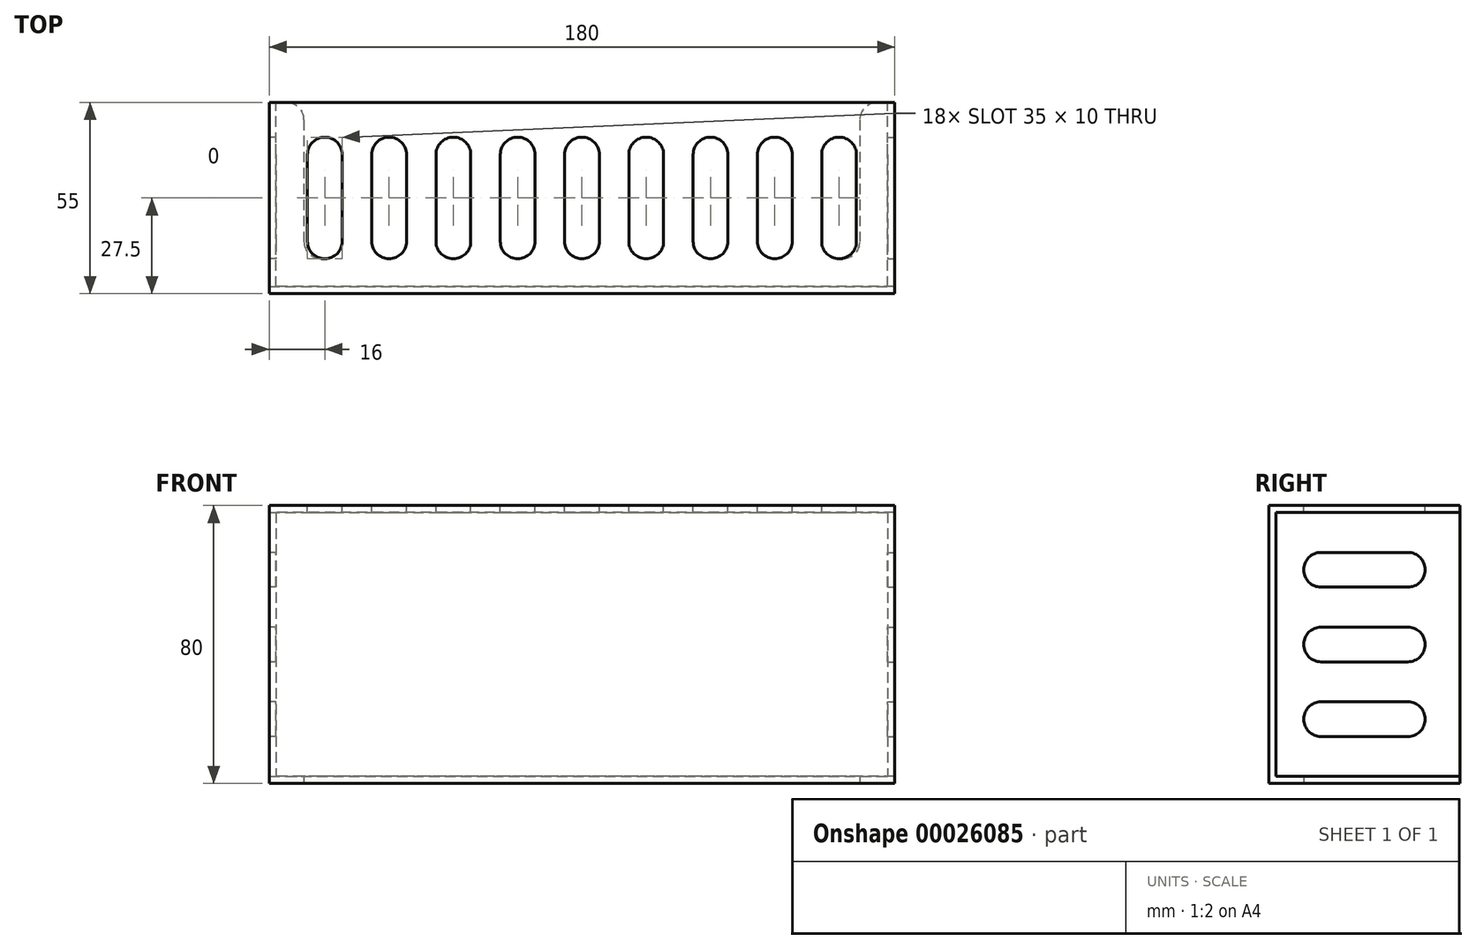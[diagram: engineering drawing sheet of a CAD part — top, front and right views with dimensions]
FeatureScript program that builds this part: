
annotation { "Feature Type Name" : "Feature", "Feature Type Description" : "" }
export const myFeature = defineFeature(function(context is Context, id is Id, definition is map)
    precondition{}
    {
        {
            var Q0;
            Q0=qCreatedBy(makeId("Top.planeOp"),FACE);
            var sketch = newSketch(context, id + "F0", { "sketchPlane" : qUnion([Q0])});
            skLineSegment(sketch, "E0.bottom", {"start": v(0, 0) * mm, "end": v(5, 0) * mm});
            skLineSegment(sketch, "E0.top", {"start": v(0, -55) * mm, "end": v(180, -55) * mm});
            skLineSegment(sketch, "E0.left", {"start": v(0, 0) * mm, "end": v(0, -55) * mm});
            skLineSegment(sketch, "E0.right", {"start": v(180, 0) * mm, "end": v(180, -55) * mm});
            skLineSegment(sketch, "E1.0", {"start": v(10, -5) * mm, "end": v(10, -40) * mm});
            skLineSegment(sketch, "E2.0", {"start": v(170, -5) * mm, "end": v(170, -40) * mm});
            skLineSegment(sketch, "E3.0", {"start": v(15, -45) * mm, "end": v(165, -45) * mm});
            skLineSegment(sketch, "E4.trimOffspring", {"start": v(175, 0) * mm, "end": v(180, 0) * mm});
            skPoint(sketch, "E5.visualSharp", {"position": v(10, 0) * mm});
            skArc(sketch, "E5.filletArc", {"start": v(10, -5) * mm, "mid": v(8.54, -1.46) * mm, "end": v(5, 0) * mm});
            skPoint(sketch, "E6.visualSharp", {"position": v(170, 0) * mm});
            skArc(sketch, "E6.filletArc", {"start": v(175, 0) * mm, "mid": v(171.46, -1.46) * mm, "end": v(170, -5) * mm});
            skPoint(sketch, "E7.visualSharp", {"position": v(10, -45) * mm});
            skArc(sketch, "E7.filletArc", {"start": v(10, -40) * mm, "mid": v(11.46, -43.54) * mm, "end": v(15, -45) * mm});
            skPoint(sketch, "E8.visualSharp", {"position": v(170, -45) * mm});
            skArc(sketch, "E8.filletArc", {"start": v(165, -45) * mm, "mid": v(168.54, -43.54) * mm, "end": v(170, -40) * mm});
            skSolve(sketch);
        }
        {
            var Q0;
            Q0=makeQuery(id+"F0.imprint","IMPRINT",FACE,{"disambiguationData":[TD([[makeQuery(id+"F0.imprint","IMPRINT",EDGE,{"derivedFrom":sQuery(id+"F0.wireOp",EDGE,"E0.bottom")}),-1.0]])]});
            extrude(context, id + "F1", {"entities" : qUnion([Q0]), "depth" : 2 * mm});
        }
        {
            var Q0;
            Q0=makeQuery(id+"F1.opExtrude","SWEPT_FACE",FACE,{"disambiguationData":[OSD([sQuery(id+"F0.wireOp",EDGE,"E0.top")])]});
            var sketch = newSketch(context, id + "F2", { "sketchPlane" : qUnion([Q0])});
            skLineSegment(sketch, "E9.0", {"start": v(0, 2) * mm, "end": v(0, 0) * mm});
            skLineSegment(sketch, "E10.0", {"start": v(0, 0) * mm, "end": v(180, 0) * mm});
            skLineSegment(sketch, "E11.0", {"start": v(180, 2) * mm, "end": v(180, 0) * mm});
            skLineSegment(sketch, "E12.top", {"start": v(0, 80) * mm, "end": v(180, 80) * mm});
            skLineSegment(sketch, "E12.left", {"start": v(0, 0) * mm, "end": v(0, 80) * mm});
            skLineSegment(sketch, "E12.right", {"start": v(180, 0) * mm, "end": v(180, 80) * mm});
            skSolve(sketch);
        }
        {
            var Q0;
            {var subQ1=sQuery(id+"F2.wireOp",EDGE,"E12.top");Q0=makeQuery(id+"F2.imprint","IMPRINT",FACE,{"disambiguationData":[TD([[makeQuery(id+"F2.imprint","IMPRINT",EDGE,{"derivedFrom":subQ1}),-1.0]])]});}
            var Q1;
            {var subQ2=sQuery(id+"F2.wireOp",EDGE,"E10.0");Q1=makeQuery(id+"F2.imprint","IMPRINT",FACE,{"disambiguationData":[TD([[makeQuery(id+"F2.imprint","IMPRINT",EDGE,{"derivedFrom":subQ2}),1.0]])]});}
            extrude(context, id + "F3", {"entities" : qUnion([Q0, Q1]), "oppositeDirection" : true, "depth" : 2 * mm});
        }
        {
            var Q0;
            Q0=makeQuery(id+"F3.opExtrude","SWEPT_FACE",FACE,{"disambiguationData":[OSD([sQuery(id+"F2.wireOp",EDGE,"E12.top")])]});
            var sketch = newSketch(context, id + "F4", { "sketchPlane" : qUnion([Q0])});
            skLineSegment(sketch, "E13.0", {"start": v(180, -55) * mm, "end": v(180, -53) * mm});
            skLineSegment(sketch, "E14.0", {"start": v(180, -53) * mm, "end": v(0, -53) * mm});
            skLineSegment(sketch, "E15.0", {"start": v(0, -55) * mm, "end": v(0, -53) * mm});
            skLineSegment(sketch, "E16.bottom", {"start": v(0, -53) * mm, "end": v(180, -53) * mm});
            skLineSegment(sketch, "E16.top", {"start": v(0, 0) * mm, "end": v(180, 0) * mm});
            skLineSegment(sketch, "E16.left", {"start": v(0, -53) * mm, "end": v(0, 0) * mm});
            skLineSegment(sketch, "E16.right", {"start": v(180, -53) * mm, "end": v(180, 0) * mm});
            skLineSegment(sketch, "E17", {"start": v(90, 0) * mm, "end": v(90, -55) * mm, "construction": true});
            skLineSegment(sketch, "E18.0", {"start": v(0, -10) * mm, "end": v(180, -10) * mm, "construction": true});
            skLineSegment(sketch, "E19.0", {"start": v(0, -45) * mm, "end": v(180, -45) * mm, "construction": true});
            skLineSegment(sketch, "E20.0", {"start": v(10, -53) * mm, "end": v(10, 0) * mm, "construction": true});
            skLineSegment(sketch, "E21.0", {"start": v(170, -53) * mm, "end": v(170, 0) * mm, "construction": true});
            skLineSegment(sketch, "E22.0", {"start": v(85, -15) * mm, "end": v(85, -40) * mm});
            skLineSegment(sketch, "E23.0", {"start": v(95, -15) * mm, "end": v(95, -40) * mm});
            skLineSegment(sketch, "E24", {"start": v(90, -10) * mm, "end": v(90, -10) * mm});
            skLineSegment(sketch, "E25", {"start": v(90, -45) * mm, "end": v(90, -45) * mm});
            skArc(sketch, "E26.filletArc", {"start": v(95, -15) * mm, "mid": v(93.54, -11.46) * mm, "end": v(90, -10) * mm});
            skArc(sketch, "E27.filletArc", {"start": v(90, -10) * mm, "mid": v(86.46, -11.46) * mm, "end": v(85, -15) * mm});
            skArc(sketch, "E28.filletArc", {"start": v(90, -45) * mm, "mid": v(93.54, -43.54) * mm, "end": v(95, -40) * mm});
            skArc(sketch, "E29.filletArc", {"start": v(85, -40) * mm, "mid": v(86.46, -43.54) * mm, "end": v(90, -45) * mm});
            skArc(sketch, "E30.1.0.0", {"start": v(108.5, -10) * mm, "mid": v(104.96, -11.46) * mm, "end": v(103.5, -15) * mm});
            skArc(sketch, "E30.1.0.1", {"start": v(113.5, -15) * mm, "mid": v(112.04, -11.46) * mm, "end": v(108.5, -10) * mm});
            skLineSegment(sketch, "E30.1.0.2", {"start": v(113.5, -15) * mm, "end": v(113.5, -40) * mm});
            skArc(sketch, "E30.1.0.3", {"start": v(108.5, -45) * mm, "mid": v(112.04, -43.54) * mm, "end": v(113.5, -40) * mm});
            skArc(sketch, "E30.1.0.4", {"start": v(103.5, -40) * mm, "mid": v(104.96, -43.54) * mm, "end": v(108.5, -45) * mm});
            skLineSegment(sketch, "E30.1.0.5", {"start": v(103.5, -15) * mm, "end": v(103.5, -40) * mm});
            skArc(sketch, "E30.2.0.0", {"start": v(127, -10) * mm, "mid": v(123.46, -11.46) * mm, "end": v(122, -15) * mm});
            skArc(sketch, "E30.2.0.1", {"start": v(132, -15) * mm, "mid": v(130.54, -11.46) * mm, "end": v(127, -10) * mm});
            skLineSegment(sketch, "E30.2.0.2", {"start": v(132, -15) * mm, "end": v(132, -40) * mm});
            skArc(sketch, "E30.2.0.3", {"start": v(127, -45) * mm, "mid": v(130.54, -43.54) * mm, "end": v(132, -40) * mm});
            skArc(sketch, "E30.2.0.4", {"start": v(122, -40) * mm, "mid": v(123.46, -43.54) * mm, "end": v(127, -45) * mm});
            skLineSegment(sketch, "E30.2.0.5", {"start": v(122, -15) * mm, "end": v(122, -40) * mm});
            skArc(sketch, "E30.3.0.0", {"start": v(145.5, -10) * mm, "mid": v(141.96, -11.46) * mm, "end": v(140.5, -15) * mm});
            skArc(sketch, "E30.3.0.1", {"start": v(150.5, -15) * mm, "mid": v(149.04, -11.46) * mm, "end": v(145.5, -10) * mm});
            skLineSegment(sketch, "E30.3.0.2", {"start": v(150.5, -15) * mm, "end": v(150.5, -40) * mm});
            skArc(sketch, "E30.3.0.3", {"start": v(145.5, -45) * mm, "mid": v(149.04, -43.54) * mm, "end": v(150.5, -40) * mm});
            skArc(sketch, "E30.3.0.4", {"start": v(140.5, -40) * mm, "mid": v(141.96, -43.54) * mm, "end": v(145.5, -45) * mm});
            skLineSegment(sketch, "E30.3.0.5", {"start": v(140.5, -15) * mm, "end": v(140.5, -40) * mm});
            skArc(sketch, "E30.4.0.0", {"start": v(164, -10) * mm, "mid": v(160.46, -11.46) * mm, "end": v(159, -15) * mm});
            skArc(sketch, "E30.4.0.1", {"start": v(169, -15) * mm, "mid": v(167.54, -11.46) * mm, "end": v(164, -10) * mm});
            skLineSegment(sketch, "E30.4.0.2", {"start": v(169, -15) * mm, "end": v(169, -40) * mm});
            skArc(sketch, "E30.4.0.3", {"start": v(164, -45) * mm, "mid": v(167.54, -43.54) * mm, "end": v(169, -40) * mm});
            skArc(sketch, "E30.4.0.4", {"start": v(159, -40) * mm, "mid": v(160.46, -43.54) * mm, "end": v(164, -45) * mm});
            skLineSegment(sketch, "E30.4.0.5", {"start": v(159, -15) * mm, "end": v(159, -40) * mm});
            skLineSegment(sketch, "E30.direction1", {"start": v(85, -15) * mm, "end": v(103.5, -15) * mm, "construction": true});
            skArc(sketch, "E31.1.0.0", {"start": v(71.5, -10) * mm, "mid": v(67.96, -11.46) * mm, "end": v(66.5, -15) * mm});
            skArc(sketch, "E31.1.0.1", {"start": v(76.5, -15) * mm, "mid": v(75.04, -11.46) * mm, "end": v(71.5, -10) * mm});
            skLineSegment(sketch, "E31.1.0.2", {"start": v(76.5, -15) * mm, "end": v(76.5, -40) * mm});
            skArc(sketch, "E31.1.0.3", {"start": v(71.5, -45) * mm, "mid": v(75.04, -43.54) * mm, "end": v(76.5, -40) * mm});
            skArc(sketch, "E31.1.0.4", {"start": v(66.5, -40) * mm, "mid": v(67.96, -43.54) * mm, "end": v(71.5, -45) * mm});
            skLineSegment(sketch, "E31.1.0.5", {"start": v(66.5, -15) * mm, "end": v(66.5, -40) * mm});
            skArc(sketch, "E31.2.0.0", {"start": v(53, -10) * mm, "mid": v(49.46, -11.46) * mm, "end": v(48, -15) * mm});
            skArc(sketch, "E31.2.0.1", {"start": v(58, -15) * mm, "mid": v(56.54, -11.46) * mm, "end": v(53, -10) * mm});
            skLineSegment(sketch, "E31.2.0.2", {"start": v(58, -15) * mm, "end": v(58, -40) * mm});
            skArc(sketch, "E31.2.0.3", {"start": v(53, -45) * mm, "mid": v(56.54, -43.54) * mm, "end": v(58, -40) * mm});
            skArc(sketch, "E31.2.0.4", {"start": v(48, -40) * mm, "mid": v(49.46, -43.54) * mm, "end": v(53, -45) * mm});
            skLineSegment(sketch, "E31.2.0.5", {"start": v(48, -15) * mm, "end": v(48, -40) * mm});
            skArc(sketch, "E31.3.0.0", {"start": v(34.5, -10) * mm, "mid": v(30.96, -11.46) * mm, "end": v(29.5, -15) * mm});
            skArc(sketch, "E31.3.0.1", {"start": v(39.5, -15) * mm, "mid": v(38.04, -11.46) * mm, "end": v(34.5, -10) * mm});
            skLineSegment(sketch, "E31.3.0.2", {"start": v(39.5, -15) * mm, "end": v(39.5, -40) * mm});
            skArc(sketch, "E31.3.0.3", {"start": v(34.5, -45) * mm, "mid": v(38.04, -43.54) * mm, "end": v(39.5, -40) * mm});
            skArc(sketch, "E31.3.0.4", {"start": v(29.5, -40) * mm, "mid": v(30.96, -43.54) * mm, "end": v(34.5, -45) * mm});
            skLineSegment(sketch, "E31.3.0.5", {"start": v(29.5, -15) * mm, "end": v(29.5, -40) * mm});
            skArc(sketch, "E31.4.0.0", {"start": v(16, -10) * mm, "mid": v(12.46, -11.46) * mm, "end": v(11, -15) * mm});
            skArc(sketch, "E31.4.0.1", {"start": v(21, -15) * mm, "mid": v(19.54, -11.46) * mm, "end": v(16, -10) * mm});
            skLineSegment(sketch, "E31.4.0.2", {"start": v(21, -15) * mm, "end": v(21, -40) * mm});
            skArc(sketch, "E31.4.0.3", {"start": v(16, -45) * mm, "mid": v(19.54, -43.54) * mm, "end": v(21, -40) * mm});
            skArc(sketch, "E31.4.0.4", {"start": v(11, -40) * mm, "mid": v(12.46, -43.54) * mm, "end": v(16, -45) * mm});
            skLineSegment(sketch, "E31.4.0.5", {"start": v(11, -15) * mm, "end": v(11, -40) * mm});
            skLineSegment(sketch, "E31.direction1", {"start": v(85, -15) * mm, "end": v(66.5, -15) * mm, "construction": true});
            skSolve(sketch);
        }
        {
            var Q0;
            {var subQ2=sQuery(id+"F4.wireOp",EDGE,"E16.top");Q0=makeQuery(id+"F4.imprint","IMPRINT",FACE,{"disambiguationData":[TD([[makeQuery(id+"F4.imprint","IMPRINT",EDGE,{"derivedFrom":subQ2}),-1.0]])]});}
            var Q1;
            {var subQ2=sQuery(id+"F4.wireOp",EDGE,"E16.bottom");Q1=makeQuery(id+"F4.imprint","IMPRINT",FACE,{"disambiguationData":[TD([[makeQuery(id+"F4.imprint","IMPRINT",EDGE,{"derivedFrom":subQ2}),1.0]])]});}
            extrude(context, id + "F5", {"entities" : qUnion([Q0, Q1]), "operationType" : NewBodyOperationType.ADD, "oppositeDirection" : true, "depth" : 2 * mm});
        }
        {
            var Q0;
            Q0=makeQuery(id+"F5.boolean.opBoolean","MERGE",FACE,{"derivedFrom":[makeQuery(id+"F3.opExtrude","SWEPT_FACE",FACE,{"disambiguationData":[OSD([sQuery(id+"F2.wireOp",EDGE,"E12.right")])]}),makeQuery(id+"F5.opExtrude","SWEPT_FACE",FACE,{"disambiguationData":[OSD([sQuery(id+"F4.wireOp",EDGE,"E16.right")])]})]});
            var sketch = newSketch(context, id + "F6", { "sketchPlane" : qUnion([Q0])});
            skPoint(sketch, "E32.0", {"position": v(0, 78) * mm});
            skPoint(sketch, "E33.0", {"position": v(-53, 78) * mm});
            skPoint(sketch, "E34.0", {"position": v(-53, 0) * mm});
            skLineSegment(sketch, "E35.top", {"start": v(0, 0) * mm, "end": v(-54.92, 0) * mm});
            skLineSegment(sketch, "E35.left", {"start": v(0, 80) * mm, "end": v(0, 0) * mm});
            skPoint(sketch, "E36.0", {"position": v(0, 80) * mm});
            skPoint(sketch, "E37.0", {"position": v(-55, 80) * mm});
            skPoint(sketch, "E38.0", {"position": v(-55, 0) * mm});
            skLineSegment(sketch, "E39", {"start": v(0, 80) * mm, "end": v(-55, 80) * mm});
            skLineSegment(sketch, "E40", {"start": v(-55, 80) * mm, "end": v(-54.92, 0) * mm});
            skLineSegment(sketch, "E41.0", {"start": v(-10, 80) * mm, "end": v(-10, 0) * mm, "construction": true});
            skLineSegment(sketch, "E42.0", {"start": v(-45, 80) * mm, "end": v(-44.92, 0) * mm, "construction": true});
            skLineSegment(sketch, "E43.0", {"start": v(0, 70) * mm, "end": v(-55, 70) * mm, "construction": true});
            skLineSegment(sketch, "E44.0", {"start": v(0, 10) * mm, "end": v(-54.92, 10) * mm, "construction": true});
            skLineSegment(sketch, "E45", {"start": v(0, 40) * mm, "end": v(-54.96, 40) * mm, "construction": true});
            skLineSegment(sketch, "E46.0", {"start": v(-15, 45) * mm, "end": v(-39.96, 45) * mm});
            skLineSegment(sketch, "E47.0", {"start": v(-15, 35) * mm, "end": v(-39.96, 35) * mm});
            skLineSegment(sketch, "E48", {"start": v(-10, 40) * mm, "end": v(-10, 40) * mm});
            skLineSegment(sketch, "E49", {"start": v(-44.96, 40) * mm, "end": v(-44.96, 40) * mm});
            skArc(sketch, "E50.filletArc", {"start": v(-10, 40) * mm, "mid": v(-11.46, 43.54) * mm, "end": v(-15, 45) * mm});
            skArc(sketch, "E51.filletArc", {"start": v(-15, 35) * mm, "mid": v(-11.46, 36.46) * mm, "end": v(-10, 40) * mm});
            skArc(sketch, "E52.filletArc", {"start": v(-39.96, 45) * mm, "mid": v(-43.5, 43.53) * mm, "end": v(-44.96, 40) * mm});
            skArc(sketch, "E53.filletArc", {"start": v(-44.96, 40) * mm, "mid": v(-43.5, 36.46) * mm, "end": v(-39.96, 35) * mm});
            skArc(sketch, "E54.0.1.0", {"start": v(-10, 61.5) * mm, "mid": v(-11.46, 65.04) * mm, "end": v(-15, 66.5) * mm});
            skArc(sketch, "E54.0.1.1", {"start": v(-15, 56.5) * mm, "mid": v(-11.46, 57.96) * mm, "end": v(-10, 61.5) * mm});
            skLineSegment(sketch, "E54.0.1.2", {"start": v(-15, 56.5) * mm, "end": v(-39.96, 56.5) * mm});
            skArc(sketch, "E54.0.1.3", {"start": v(-44.96, 61.5) * mm, "mid": v(-43.5, 57.96) * mm, "end": v(-39.96, 56.5) * mm});
            skArc(sketch, "E54.0.1.4", {"start": v(-39.96, 66.5) * mm, "mid": v(-43.5, 65.03) * mm, "end": v(-44.96, 61.5) * mm});
            skLineSegment(sketch, "E54.0.1.5", {"start": v(-15, 66.5) * mm, "end": v(-39.96, 66.5) * mm});
            skLineSegment(sketch, "E54.direction1", {"start": v(-15, 40) * mm, "end": v(10.4, 40) * mm, "construction": true});
            skLineSegment(sketch, "E54.direction2", {"start": v(-15, 40) * mm, "end": v(-15, 61.5) * mm, "construction": true});
            skArc(sketch, "E55.0.1.0", {"start": v(-15, 13.5) * mm, "mid": v(-11.46, 14.96) * mm, "end": v(-10, 18.5) * mm});
            skLineSegment(sketch, "E55.0.1.1", {"start": v(-15, 13.5) * mm, "end": v(-39.96, 13.5) * mm});
            skArc(sketch, "E55.0.1.2", {"start": v(-44.96, 18.5) * mm, "mid": v(-43.5, 14.96) * mm, "end": v(-39.96, 13.5) * mm});
            skArc(sketch, "E55.0.1.3", {"start": v(-39.96, 23.5) * mm, "mid": v(-43.5, 22.03) * mm, "end": v(-44.96, 18.5) * mm});
            skLineSegment(sketch, "E55.0.1.4", {"start": v(-15, 23.5) * mm, "end": v(-39.96, 23.5) * mm});
            skArc(sketch, "E55.0.1.5", {"start": v(-10, 18.5) * mm, "mid": v(-11.46, 22.04) * mm, "end": v(-15, 23.5) * mm});
            skLineSegment(sketch, "E55.direction1", {"start": v(-15, 35) * mm, "end": v(10.4, 35) * mm, "construction": true});
            skLineSegment(sketch, "E55.direction2", {"start": v(-15, 35) * mm, "end": v(-15, 13.5) * mm, "construction": true});
            skSolve(sketch);
        }
        {
            var Q0;
            {var subQ1=makeQuery(id+"F3.opExtrude","CAP_EDGE",EDGE,{"disambiguationData":[OSD([sQuery(id+"F2.wireOp",EDGE,"E12.right")])],"isStart":true});Q0=makeQuery(id+"F6.imprint","IMPRINT",FACE,{"disambiguationData":[TD([[makeQuery(id+"F6.imprint","IMPRINT",EDGE,{"derivedFrom":subQ1}),-1.0]])]});}
            var Q1;
            {var subQ1=makeQuery(id+"F5.opExtrude","CAP_EDGE",EDGE,{"disambiguationData":[OSD([sQuery(id+"F4.wireOp",EDGE,"E16.right")])],"isStart":false});Q1=makeQuery(id+"F6.imprint","IMPRINT",FACE,{"disambiguationData":[TD([[makeQuery(id+"F6.imprint","IMPRINT",EDGE,{"derivedFrom":subQ1}),-1.0]])]});}
            extrude(context, id + "F7", {"entities" : qUnion([Q0, Q1]), "operationType" : NewBodyOperationType.ADD, "oppositeDirection" : true, "depth" : 2 * mm});
        }
        {
            var Q0;
            {var subQ0=sQuery(id+"F2.wireOp",EDGE,"E12.right");Q0=makeQuery(id+"F7.boolean.opBoolean","MERGE",FACE,{"derivedFrom":[makeQuery(id+"F1.opExtrude","SWEPT_FACE",FACE,{"disambiguationData":[OSD([sQuery(id+"F0.wireOp",EDGE,"E0.right")])]}),makeQuery(id+"F7.opExtrude","CAP_FACE",FACE,{"disambiguationData":[OSD([subQ0,sQuery(id+"F4.wireOp",EDGE,"E16.right"),sQuery(id+"F6.wireOp",EDGE,"E35.top"),sQuery(id+"F6.wireOp",EDGE,"E35.left"),sQuery(id+"F6.wireOp",EDGE,"E46.0"),sQuery(id+"F6.wireOp",EDGE,"E47.0"),sQuery(id+"F6.wireOp",EDGE,"E50.filletArc"),sQuery(id+"F6.wireOp",EDGE,"E51.filletArc"),sQuery(id+"F6.wireOp",EDGE,"E52.filletArc"),sQuery(id+"F6.wireOp",EDGE,"E53.filletArc"),sQuery(id+"F6.wireOp",EDGE,"E54.0.1.0"),sQuery(id+"F6.wireOp",EDGE,"E54.0.1.1"),sQuery(id+"F6.wireOp",EDGE,"E54.0.1.2"),sQuery(id+"F6.wireOp",EDGE,"E54.0.1.3"),sQuery(id+"F6.wireOp",EDGE,"E54.0.1.4"),sQuery(id+"F6.wireOp",EDGE,"E54.0.1.5"),sQuery(id+"F6.wireOp",EDGE,"E55.0.1.0"),sQuery(id+"F6.wireOp",EDGE,"E55.0.1.1"),sQuery(id+"F6.wireOp",EDGE,"E55.0.1.2"),sQuery(id+"F6.wireOp",EDGE,"E55.0.1.3"),sQuery(id+"F6.wireOp",EDGE,"E55.0.1.4"),sQuery(id+"F6.wireOp",EDGE,"E55.0.1.5")])],"isStart":true}),makeQuery(id+"F7.opExtrude","CAP_FACE",FACE,{"disambiguationData":[OSD([sQuery(id+"F2.wireOp",EDGE,"E10.0"),subQ0,sQuery(id+"F6.wireOp",EDGE,"E40")])],"isStart":true})]});}
            cPlane(context, id + "F8", {"entities" : qUnion([Q0]), "cplaneType" : CPlaneType.OFFSET, "offset" : 90 * mm, "oppositeDirection" : true, "width" : 152.4 * mm, "height" : 152.4 * mm});
        }
        {
            var Q0;
            Q0=makeQuery(id+"F1.opExtrude","SWEPT_BODY",BODY,{"disambiguationData":[OSD([sQuery(id+"F0.wireOp",EDGE,"E0.bottom"),sQuery(id+"F0.wireOp",EDGE,"E0.top"),sQuery(id+"F0.wireOp",EDGE,"E0.left"),sQuery(id+"F0.wireOp",EDGE,"E0.right"),sQuery(id+"F0.wireOp",EDGE,"E1.0"),sQuery(id+"F0.wireOp",EDGE,"E2.0"),sQuery(id+"F0.wireOp",EDGE,"E3.0"),sQuery(id+"F0.wireOp",EDGE,"E4.trimOffspring")])]});
            var Q1;
            Q1=qCreatedBy(id+"F8.planeOp",FACE);
            mirror(context, id + "F9", {"entities" : qUnion([Q0]), "mirrorPlane" : qUnion([Q1])});
        }
    });
